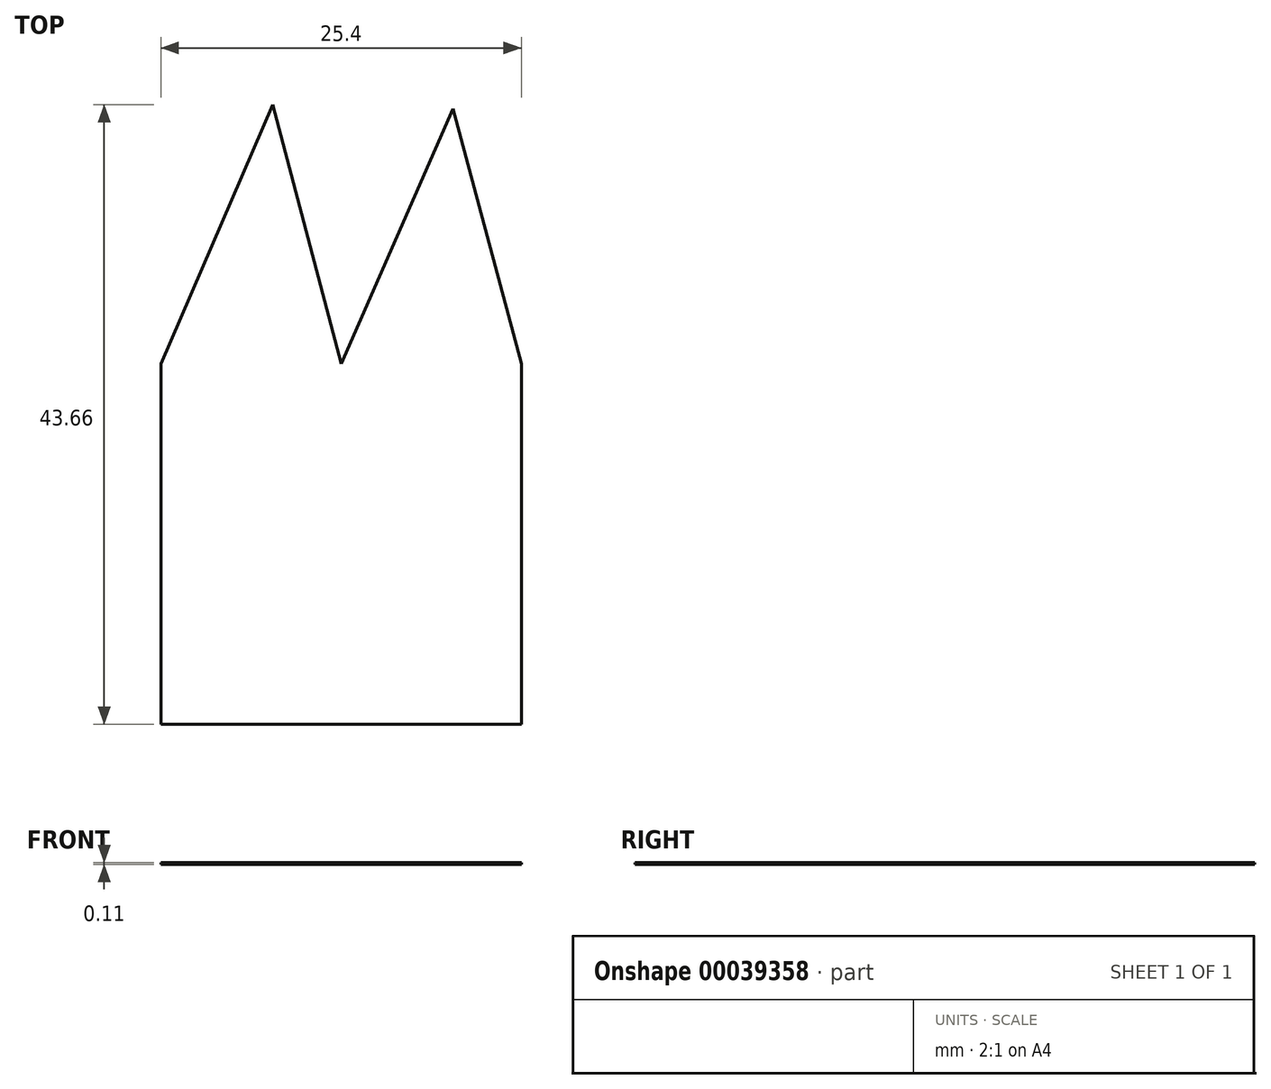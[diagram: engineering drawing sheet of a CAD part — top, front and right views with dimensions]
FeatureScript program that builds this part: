
annotation { "Feature Type Name" : "Feature", "Feature Type Description" : "" }
export const myFeature = defineFeature(function(context is Context, id is Id, definition is map)
    precondition{}
    {
        {
            var Q0;
            Q0=qCreatedBy(makeId("Top.planeOp"),FACE);
            var sketch = newSketch(context, id + "F0", { "sketchPlane" : qUnion([Q0])});
            skLineSegment(sketch, "E0.rect.bottom", {"start": v(12.7, -12.7) * mm, "end": v(-12.7, -12.7) * mm});
            skLineSegment(sketch, "E0.rect.top", {"start": v(12.7, 12.7) * mm, "end": v(-12.7, 12.7) * mm});
            skLineSegment(sketch, "E0.rect.left", {"start": v(12.7, -12.7) * mm, "end": v(12.7, 12.7) * mm});
            skLineSegment(sketch, "E0.rect.right", {"start": v(-12.7, -12.7) * mm, "end": v(-12.7, 12.7) * mm});
            skPoint(sketch, "E0.rect.middle", {"position": v(0, 0) * mm});
            skLineSegment(sketch, "E1", {"start": v(-12.7, 12.7) * mm, "end": v(-4.82, 30.96) * mm});
            skLineSegment(sketch, "E2", {"start": v(-4.82, 30.96) * mm, "end": v(0, 12.7) * mm});
            skLineSegment(sketch, "E3", {"start": v(0, 0) * mm, "end": v(0, 59.44) * mm});
            skLineSegment(sketch, "E4", {"start": v(0, 12.7) * mm, "end": v(7.9, 30.68) * mm});
            skLineSegment(sketch, "E5", {"start": v(7.9, 30.68) * mm, "end": v(12.7, 12.7) * mm});
            skSolve(sketch);
        }
        {
            var Q0;
            {var subQ1=sQuery(id+"F0.wireOp",EDGE,"E1");Q0=makeQuery(id+"F0.imprint","IMPRINT",FACE,{"disambiguationData":[TD([[makeQuery(id+"F0.imprint","IMPRINT",EDGE,{"derivedFrom":subQ1}),-1.0]])]});}
            var Q1;
            {var subQ1=sQuery(id+"F0.wireOp",EDGE,"E4");Q1=makeQuery(id+"F0.imprint","IMPRINT",FACE,{"disambiguationData":[TD([[makeQuery(id+"F0.imprint","IMPRINT",EDGE,{"derivedFrom":subQ1}),-1.0]])]});}
            var Q2;
            Q2=makeQuery(id+"F0.imprint","IMPRINT",FACE,{"disambiguationData":[TD([[makeQuery(id+"F0.imprint","IMPRINT",EDGE,{"derivedFrom":sQuery(id+"F0.wireOp",EDGE,"E0.rect.bottom")}),-1.0]])]});
            extrude(context, id + "F1", {"entities" : qUnion([Q0, Q1, Q2]), "depth" : 0.1 * mm});
        }
    });
